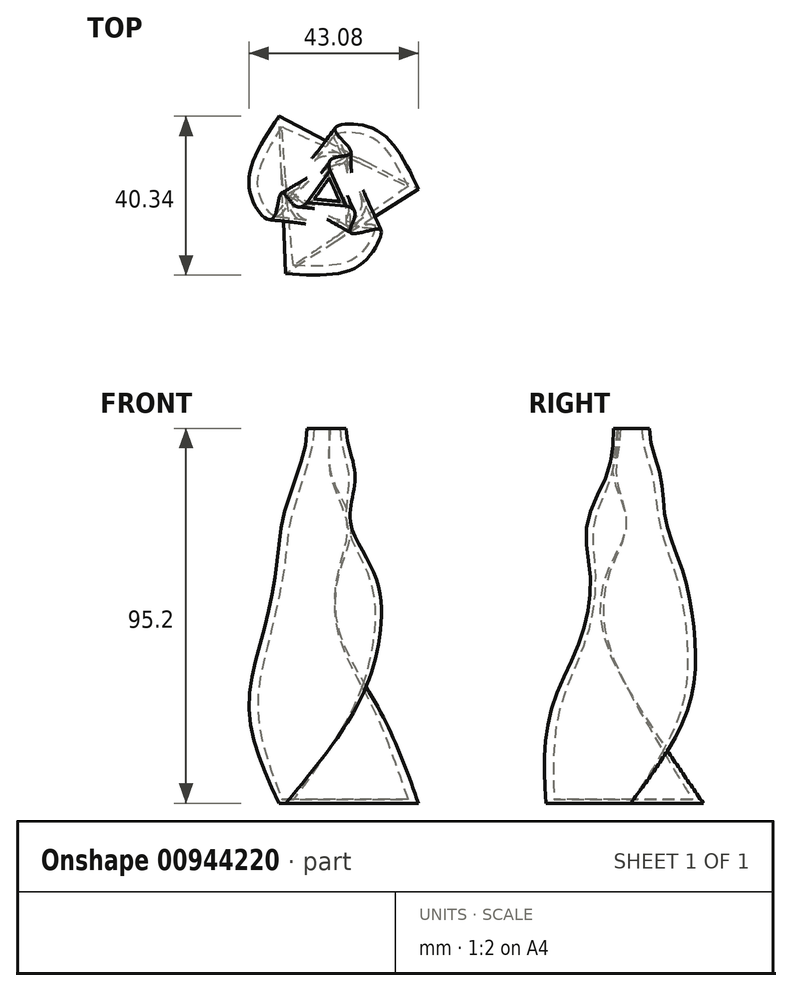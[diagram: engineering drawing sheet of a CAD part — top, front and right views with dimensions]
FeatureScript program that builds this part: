
annotation { "Feature Type Name" : "Feature", "Feature Type Description" : "" }
export const myFeature = defineFeature(function(context is Context, id is Id, definition is map)
    precondition{}
    {
        {
            var Q0;
            Q0=qCreatedBy(makeId("Top.planeOp"),FACE);
            cPlane(context, id + "F0", {"entities" : qUnion([Q0]), "cplaneType" : CPlaneType.OFFSET, "offset" : 71.6 * mm, "width" : 150 * mm, "height" : 150 * mm});
        }
        {
            var Q0;
            Q0=qCreatedBy(makeId("Top.planeOp"),FACE);
            cPlane(context, id + "F1", {"entities" : qUnion([Q0]), "cplaneType" : CPlaneType.OFFSET, "offset" : 25 * mm, "width" : 150 * mm, "height" : 150 * mm});
        }
        {
            var Q0;
            Q0=qCreatedBy(makeId("Top.planeOp"),FACE);
            cPlane(context, id + "F2", {"entities" : qUnion([Q0]), "cplaneType" : CPlaneType.OFFSET, "offset" : 44.2 * mm, "width" : 150 * mm, "height" : 150 * mm});
        }
        {
            var Q0;
            Q0=qCreatedBy(makeId("Top.planeOp"),FACE);
            var sketch = newSketch(context, id + "F3", { "sketchPlane" : qUnion([Q0])});
            skCircle(sketch, "E0.cCircle", {"center": v(0, 0) * mm, "radius": 11.55 * mm, "construction": true});
            skLineSegment(sketch, "E0.0", {"start": v(-12.4, 19.48) * mm, "end": v(23.07, 1) * mm});
            skLineSegment(sketch, "E0.1", {"start": v(23.07, 1) * mm, "end": v(-10.67, -20.48) * mm});
            skLineSegment(sketch, "E0.2", {"start": v(-10.67, -20.48) * mm, "end": v(-12.4, 19.48) * mm});
            skPoint(sketch, "E0.0.midPoint", {"position": v(5.33, 10.24) * mm});
            skSolve(sketch);
        }
        {
            var Q0;
            Q0=qCreatedBy(id+"F0.planeOp",FACE);
            var sketch = newSketch(context, id + "F4", { "sketchPlane" : qUnion([Q0])});
            skCircle(sketch, "E1.cCircle", {"center": v(0, 0) * mm, "radius": 5.77 * mm, "construction": true});
            skLineSegment(sketch, "E1.0", {"start": v(5.77, 10) * mm, "end": v(5.77, -10) * mm});
            skLineSegment(sketch, "E1.1", {"start": v(5.77, -10) * mm, "end": v(-11.55, 0) * mm});
            skLineSegment(sketch, "E1.2", {"start": v(-11.55, 0) * mm, "end": v(5.77, 10) * mm});
            skPoint(sketch, "E1.0.midPoint", {"position": v(5.77, 0) * mm});
            skSolve(sketch);
        }
        {
            var Q0;
            Q0=qCreatedBy(id+"F1.planeOp",FACE);
            var sketch = newSketch(context, id + "F5", { "sketchPlane" : qUnion([Q0])});
            skCircle(sketch, "E2.cCircle", {"center": v(0, 0) * mm, "radius": 10.1 * mm, "construction": true});
            skLineSegment(sketch, "E2.0", {"start": v(12.44, 15.92) * mm, "end": v(7.57, -18.74) * mm});
            skLineSegment(sketch, "E2.1", {"start": v(7.57, -18.74) * mm, "end": v(-20.01, 2.82) * mm});
            skLineSegment(sketch, "E2.2", {"start": v(-20.01, 2.82) * mm, "end": v(12.44, 15.92) * mm});
            skPoint(sketch, "E2.0.midPoint", {"position": v(10, -1.4) * mm});
            skSolve(sketch);
        }
        {
            var Q0;
            Q0=qCreatedBy(id+"F2.planeOp",FACE);
            cPlane(context, id + "F6", {"entities" : qUnion([Q0]), "cplaneType" : CPlaneType.OFFSET, "offset" : 14.9 * mm, "width" : 150 * mm, "height" : 150 * mm});
        }
        {
            var Q0;
            Q0=qCreatedBy(id+"F2.planeOp",FACE);
            var sketch = newSketch(context, id + "F7", { "sketchPlane" : qUnion([Q0])});
            skCircle(sketch, "E3.cCircle", {"center": v(0, 0) * mm, "radius": 8.66 * mm, "construction": true});
            skLineSegment(sketch, "E3.0", {"start": v(-16.18, -6.18) * mm, "end": v(2.73, 17.1) * mm});
            skLineSegment(sketch, "E3.1", {"start": v(2.73, 17.1) * mm, "end": v(13.44, -10.92) * mm});
            skLineSegment(sketch, "E3.2", {"start": v(13.44, -10.92) * mm, "end": v(-16.18, -6.18) * mm});
            skPoint(sketch, "E3.0.midPoint", {"position": v(-6.72, 5.46) * mm});
            skSolve(sketch);
        }
        {
            var Q0;
            Q0=qCreatedBy(id+"F6.planeOp",FACE);
            var sketch = newSketch(context, id + "F8", { "sketchPlane" : qUnion([Q0])});
            skCircle(sketch, "E4.cCircle", {"center": v(0.46, 0) * mm, "radius": 7.22 * mm, "construction": true});
            skLineSegment(sketch, "E4.0", {"start": v(3.03, 14.2) * mm, "end": v(11.48, -9.33) * mm});
            skLineSegment(sketch, "E4.1", {"start": v(11.48, -9.33) * mm, "end": v(-13.12, -4.88) * mm});
            skLineSegment(sketch, "E4.2", {"start": v(-13.12, -4.88) * mm, "end": v(3.03, 14.2) * mm});
            skPoint(sketch, "E4.0.midPoint", {"position": v(7.26, 2.44) * mm});
            skSolve(sketch);
        }
        {
            var Q0;
            Q0=qCreatedBy(id+"F0.planeOp",FACE);
            cPlane(context, id + "F9", {"entities" : qUnion([Q0]), "cplaneType" : CPlaneType.OFFSET, "offset" : 11.5 * mm, "width" : 150 * mm, "height" : 150 * mm});
        }
        {
            var Q0;
            Q0=qCreatedBy(id+"F9.planeOp",FACE);
            cPlane(context, id + "F10", {"entities" : qUnion([Q0]), "cplaneType" : CPlaneType.OFFSET, "offset" : 12.1 * mm, "width" : 150 * mm, "height" : 150 * mm});
        }
        {
            var Q0;
            Q0=qCreatedBy(id+"F9.planeOp",FACE);
            var sketch = newSketch(context, id + "F11", { "sketchPlane" : qUnion([Q0])});
            skCircle(sketch, "E5.cCircle", {"center": v(0, 0) * mm, "radius": 4.33 * mm, "construction": true});
            skLineSegment(sketch, "E5.0", {"start": v(1, 8.6) * mm, "end": v(6.94, -5.17) * mm});
            skLineSegment(sketch, "E5.1", {"start": v(6.94, -5.17) * mm, "end": v(-7.95, -3.43) * mm});
            skLineSegment(sketch, "E5.2", {"start": v(-7.95, -3.43) * mm, "end": v(1, 8.6) * mm});
            skPoint(sketch, "E5.0.midPoint", {"position": v(3.98, 1.71) * mm});
            skSolve(sketch);
        }
        {
            var Q0;
            Q0=qCreatedBy(id+"F10.planeOp",FACE);
            var sketch = newSketch(context, id + "F12", { "sketchPlane" : qUnion([Q0])});
            skCircle(sketch, "E6.cCircle", {"center": v(0, 0) * mm, "radius": 2.89 * mm, "construction": true});
            skLineSegment(sketch, "E6.0", {"start": v(-5.26, -2.4) * mm, "end": v(0.56, 5.75) * mm});
            skLineSegment(sketch, "E6.1", {"start": v(0.56, 5.75) * mm, "end": v(4.7, -3.36) * mm});
            skLineSegment(sketch, "E6.2", {"start": v(4.7, -3.36) * mm, "end": v(-5.26, -2.4) * mm});
            skPoint(sketch, "E6.0.midPoint", {"position": v(-2.35, 1.68) * mm});
            skSolve(sketch);
        }
        {
            var Q0;
            Q0=makeQuery(id+"F12.imprint","IMPRINT",FACE,{"disambiguationData":[TD([[makeQuery(id+"F12.imprint","IMPRINT",EDGE,{"derivedFrom":sQuery(id+"F12.wireOp",EDGE,"E6.0")}),-1.0]])]});
            var Q1;
            Q1=makeQuery(id+"F11.imprint","IMPRINT",FACE,{"disambiguationData":[TD([[makeQuery(id+"F11.imprint","IMPRINT",EDGE,{"derivedFrom":sQuery(id+"F11.wireOp",EDGE,"E5.0")}),-1.0]])]});
            var Q2;
            Q2=makeQuery(id+"F4.imprint","IMPRINT",FACE,{"disambiguationData":[TD([[makeQuery(id+"F4.imprint","IMPRINT",EDGE,{"derivedFrom":sQuery(id+"F4.wireOp",EDGE,"E1.0")}),-1.0]])]});
            var Q3;
            Q3=makeQuery(id+"F8.imprint","IMPRINT",FACE,{"disambiguationData":[TD([[makeQuery(id+"F8.imprint","IMPRINT",EDGE,{"derivedFrom":sQuery(id+"F8.wireOp",EDGE,"E4.0")}),-1.0]])]});
            var Q4;
            Q4=makeQuery(id+"F7.imprint","IMPRINT",FACE,{"disambiguationData":[TD([[makeQuery(id+"F7.imprint","IMPRINT",EDGE,{"derivedFrom":sQuery(id+"F7.wireOp",EDGE,"E3.0")}),-1.0]])]});
            var Q5;
            Q5=makeQuery(id+"F5.imprint","IMPRINT",FACE,{"disambiguationData":[TD([[makeQuery(id+"F5.imprint","IMPRINT",EDGE,{"derivedFrom":sQuery(id+"F5.wireOp",EDGE,"E2.0")}),-1.0]])]});
            var Q6;
            Q6=makeQuery(id+"F3.imprint","IMPRINT",FACE,{"disambiguationData":[TD([[makeQuery(id+"F3.imprint","IMPRINT",EDGE,{"derivedFrom":sQuery(id+"F3.wireOp",EDGE,"E0.0")}),-1.0]])]});
            loft(context, id + "F13", {"startCondition" : LoftEndDerivativeType.NORMAL_TO_PROFILE, "startMagnitude" : 1, "sheetProfilesArray" : [{ "sheetProfileEntities" : qUnion([Q0]) }, { "sheetProfileEntities" : qUnion([Q1]) }, { "sheetProfileEntities" : qUnion([Q2]) }, { "sheetProfileEntities" : qUnion([Q3]) }, { "sheetProfileEntities" : qUnion([Q4]) }, { "sheetProfileEntities" : qUnion([Q5]) }, { "sheetProfileEntities" : qUnion([Q6]) }]});
        }
        {
            var Q0;
            Q0=makeQuery(id+"F13.opLoft","CAP_FACE",FACE,{"disambiguationData":[OSD([makeQuery(id+"F12.imprint","IMPRINT",FACE,{"disambiguationData":[TD([[makeQuery(id+"F12.imprint","IMPRINT",EDGE,{"derivedFrom":sQuery(id+"F12.wireOp",EDGE,"E6.0")}),-1.0]])]})])],"isStart":true});
            shell(context, id + "F14", {"entities" : qUnion([Q0]), "thickness" : 1 * mm});
        }
    });
